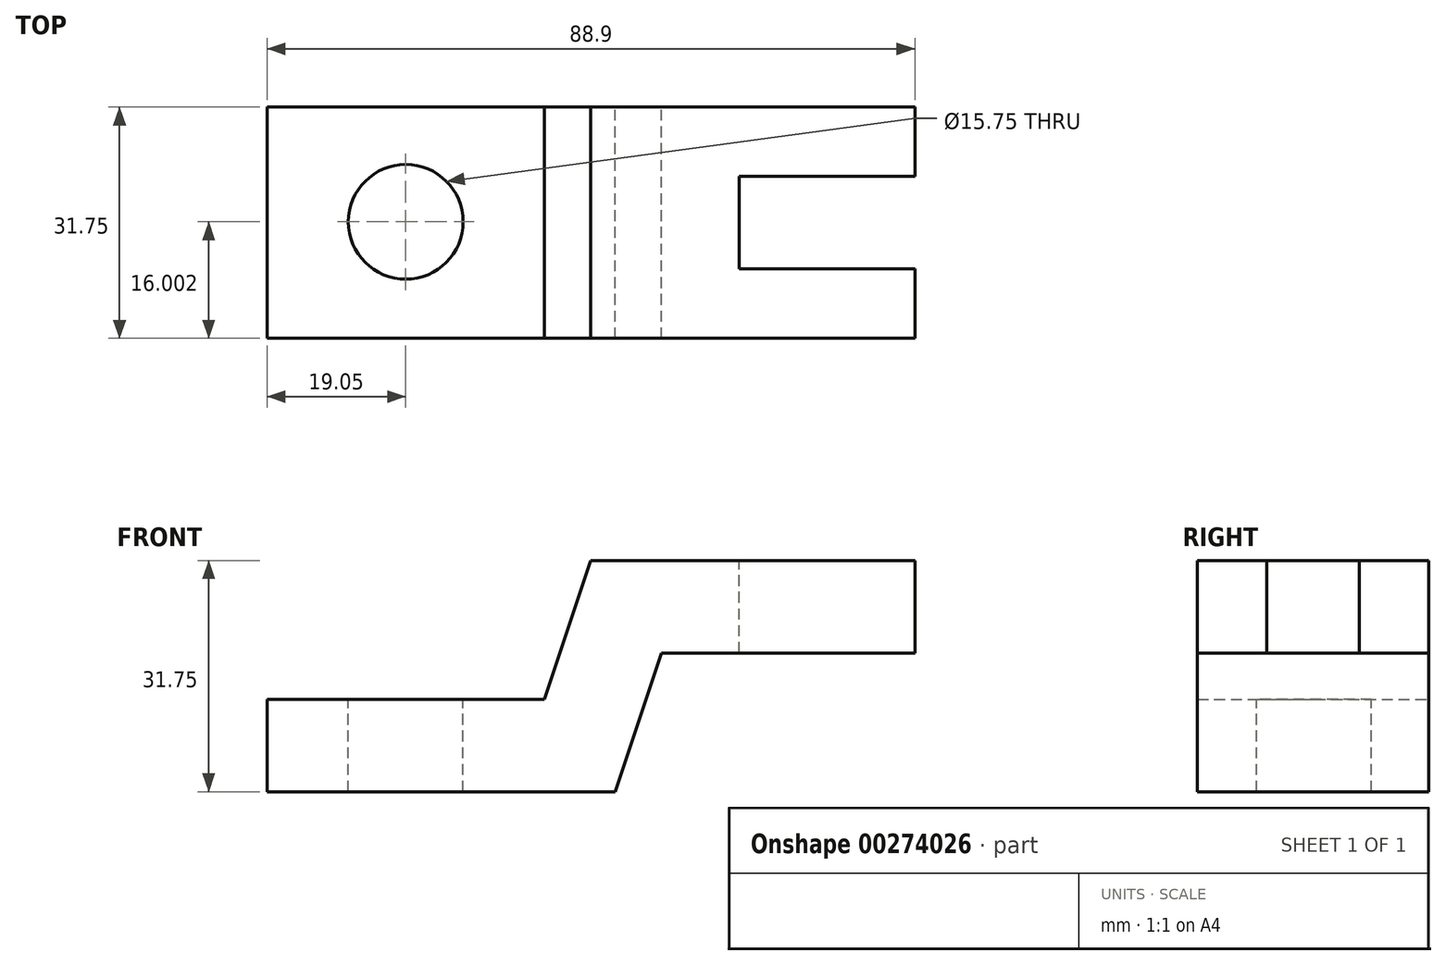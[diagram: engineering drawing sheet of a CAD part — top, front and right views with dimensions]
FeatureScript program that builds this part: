
annotation { "Feature Type Name" : "Feature", "Feature Type Description" : "" }
export const myFeature = defineFeature(function(context is Context, id is Id, definition is map)
    precondition{}
    {
        {
            var Q0;
            Q0=qCreatedBy(makeId("Front.planeOp"),FACE);
            var sketch = newSketch(context, id + "F0", { "sketchPlane" : qUnion([Q0])});
            skLineSegment(sketch, "E0", {"start": v(0, 0) * mm, "end": v(47.75, 0) * mm});
            skLineSegment(sketch, "E1", {"start": v(88.9, 19.05) * mm, "end": v(88.9, 31.75) * mm});
            skLineSegment(sketch, "E2", {"start": v(88.9, 31.75) * mm, "end": v(44.45, 31.75) * mm});
            skLineSegment(sketch, "E3", {"start": v(0, 12.7) * mm, "end": v(0, 0) * mm});
            skLineSegment(sketch, "E4", {"start": v(38.1, 12.7) * mm, "end": v(44.45, 31.75) * mm});
            skLineSegment(sketch, "E5", {"start": v(47.75, 0) * mm, "end": v(54.1, 19.05) * mm});
            skLineSegment(sketch, "E6", {"start": v(38.1, 12.7) * mm, "end": v(0, 12.7) * mm});
            skLineSegment(sketch, "E7", {"start": v(54.1, 19.05) * mm, "end": v(88.9, 19.05) * mm});
            skSolve(sketch);
        }
        {
            var Q0;
            Q0=makeQuery(id+"F0.imprint","IMPRINT",FACE,{"disambiguationData":[TD([[makeQuery(id+"F0.imprint","IMPRINT",EDGE,{"derivedFrom":sQuery(id+"F0.wireOp",EDGE,"E0")}),1.0]])]});
            extrude(context, id + "F1", {"entities" : qUnion([Q0]), "depth" : 31.75 * mm});
        }
        {
            var Q0;
            Q0=makeQuery(id+"F1.opExtrude","SWEPT_FACE",FACE,{"disambiguationData":[OSD([sQuery(id+"F0.wireOp",EDGE,"E2")])]});
            var sketch = newSketch(context, id + "F2", { "sketchPlane" : qUnion([Q0])});
            skLineSegment(sketch, "E8.0", {"start": v(88.9, -9.53) * mm, "end": v(64.77, -9.53) * mm});
            skLineSegment(sketch, "E9.0", {"start": v(64.77, -22.23) * mm, "end": v(64.77, -9.52) * mm});
            skLineSegment(sketch, "E10.0", {"start": v(88.9, -22.23) * mm, "end": v(64.77, -22.23) * mm});
            skSolve(sketch);
        }
        {
            var Q0;
            {var subQ0=sQuery(id+"F2.wireOp",EDGE,"E8.0");Q0=makeQuery(id+"F2.imprint","IMPRINT",FACE,{"disambiguationData":[TD([[makeQuery(id+"F2.imprint","IMPRINT",EDGE,{"derivedFrom":subQ0}),1.0]])]});}
            extrude(context, id + "F3", {"entities" : qUnion([Q0]), "operationType" : NewBodyOperationType.REMOVE, "oppositeDirection" : true, "depth" : 12.7 * mm});
        }
        {
            var Q0;
            Q0=makeQuery(id+"F1.opExtrude","SWEPT_FACE",FACE,{"disambiguationData":[OSD([sQuery(id+"F0.wireOp",EDGE,"E6")])]});
            var sketch = newSketch(context, id + "F4", { "sketchPlane" : qUnion([Q0])});
            skCircle(sketch, "E11", {"center": v(19.05, -15.75) * mm, "radius": 7.87 * mm});
            skSolve(sketch);
        }
        {
            var Q0;
            Q0=makeQuery(id+"F4.imprint","IMPRINT",FACE,{"disambiguationData":[TD([[makeQuery(id+"F4.imprint","IMPRINT",EDGE,{"derivedFrom":sQuery(id+"F4.wireOp",EDGE,"E11")}),1.0]])]});
            extrude(context, id + "F5", {"entities" : qUnion([Q0]), "operationType" : NewBodyOperationType.REMOVE, "oppositeDirection" : true, "depth" : 12.7 * mm});
        }
    });
